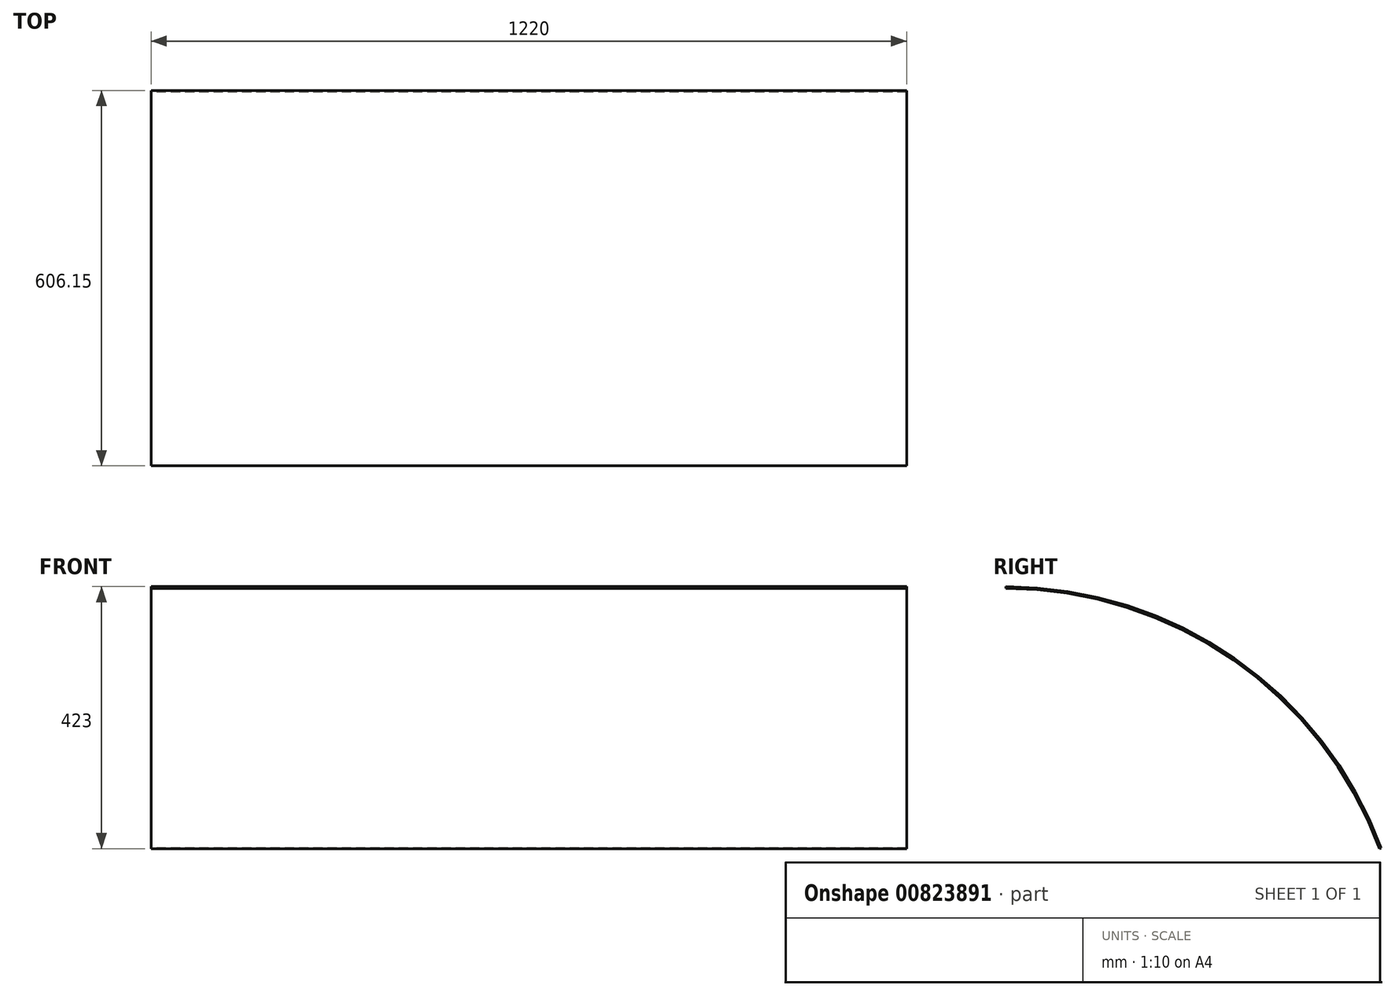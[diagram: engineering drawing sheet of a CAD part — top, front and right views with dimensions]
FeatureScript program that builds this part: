
annotation { "Feature Type Name" : "Feature", "Feature Type Description" : "" }
export const myFeature = defineFeature(function(context is Context, id is Id, definition is map)
    precondition{}
    {
        {
            var Q0;
            Q0=qCreatedBy(makeId("Right.planeOp"),FACE);
            var sketch = newSketch(context, id + "F0", { "sketchPlane" : qUnion([Q0])});
            skArc(sketch, "E0", {"start": v(167.5, -201.6) * mm, "mid": v(-68.28, 103.06) * mm, "end": v(-435.84, 218.4) * mm});
            skArc(sketch, "E1.0", {"start": v(170.3, -200.56) * mm, "mid": v(-66.57, 105.52) * mm, "end": v(-435.84, 221.4) * mm});
            skLineSegment(sketch, "E2", {"start": v(-435.84, 221.4) * mm, "end": v(-435.84, 218.4) * mm});
            skLineSegment(sketch, "E3", {"start": v(170.3, -200.56) * mm, "end": v(167.5, -201.6) * mm});
            skSolve(sketch);
        }
        {
            var Q0;
            Q0=makeQuery(id+"F0.imprint","IMPRINT",FACE,{"disambiguationData":[TD([[makeQuery(id+"F0.imprint","IMPRINT",EDGE,{"derivedFrom":sQuery(id+"F0.wireOp",EDGE,"E0")}),-1.0]])]});
            extrude(context, id + "F1", {"entities" : qUnion([Q0]), "endBound" : BoundingType.SYMMETRIC, "depth" : 1220 * mm, "offsetDistance" : 25 * mm});
        }
    });
